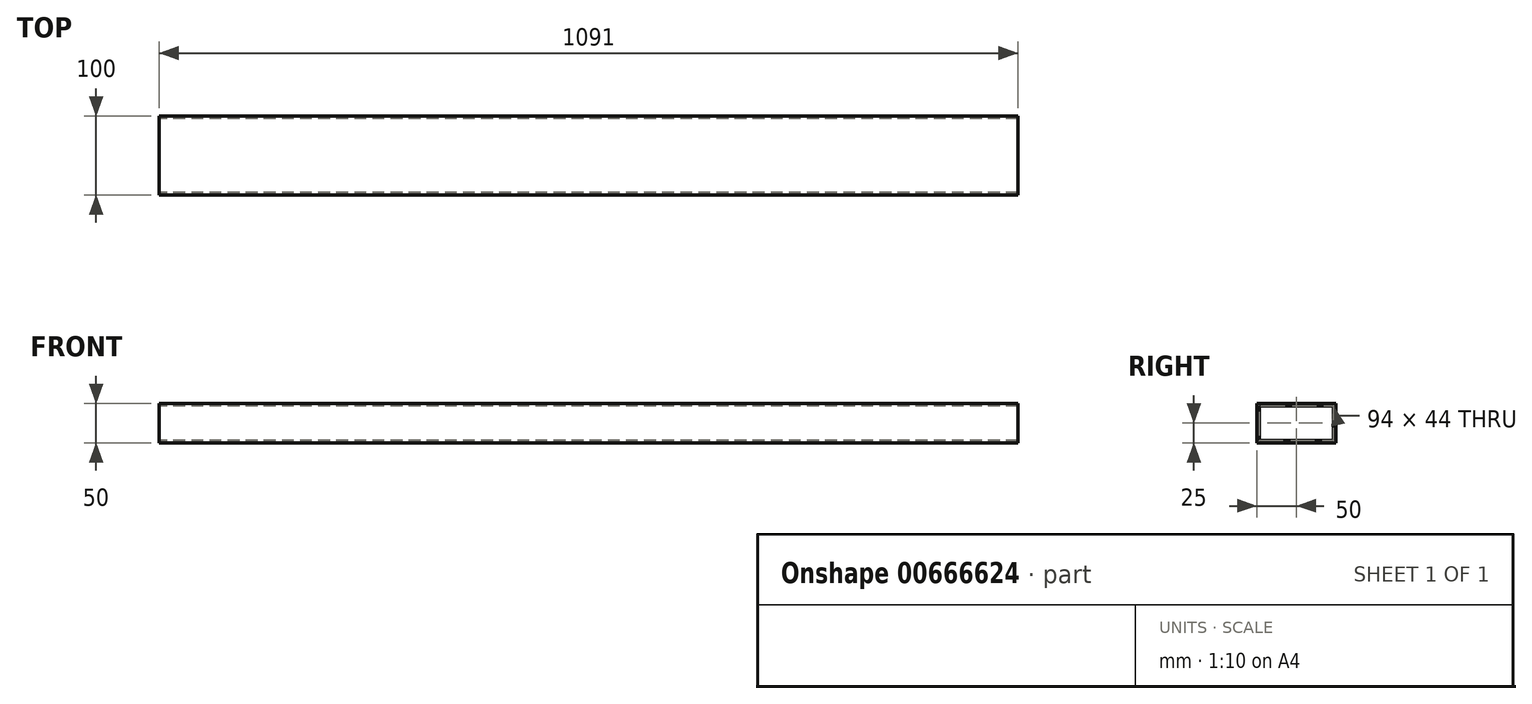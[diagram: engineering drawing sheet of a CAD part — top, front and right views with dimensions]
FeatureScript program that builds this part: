
annotation { "Feature Type Name" : "Feature", "Feature Type Description" : "" }
export const myFeature = defineFeature(function(context is Context, id is Id, definition is map)
    precondition{}
    {
        {
            var Q0;
            Q0=qCreatedBy(makeId("Right.planeOp"),FACE);
            var sketch = newSketch(context, id + "F0", { "sketchPlane" : qUnion([Q0])});
            skLineSegment(sketch, "E0.bottom", {"start": v(50, -25) * mm, "end": v(-50, -25) * mm});
            skLineSegment(sketch, "E0.top", {"start": v(50, 25) * mm, "end": v(-50, 25) * mm});
            skLineSegment(sketch, "E0.left", {"start": v(50, -25) * mm, "end": v(50, 25) * mm});
            skLineSegment(sketch, "E0.right", {"start": v(-50, -25) * mm, "end": v(-50, 25) * mm});
            skPoint(sketch, "E0.middle", {"position": v(0, 0) * mm});
            skLineSegment(sketch, "E1.bottom", {"start": v(47, -22) * mm, "end": v(-47, -22) * mm});
            skLineSegment(sketch, "E1.top", {"start": v(47, 22) * mm, "end": v(-47, 22) * mm});
            skLineSegment(sketch, "E1.left", {"start": v(47, -22) * mm, "end": v(47, 22) * mm});
            skLineSegment(sketch, "E1.right", {"start": v(-47, -22) * mm, "end": v(-47, 22) * mm});
            skSolve(sketch);
        }
        {
            var Q0;
            Q0=makeQuery(id+"F0.imprint","IMPRINT",FACE,{"disambiguationData":[TD([[makeQuery(id+"F0.imprint","IMPRINT",EDGE,{"derivedFrom":sQuery(id+"F0.wireOp",EDGE,"E0.bottom")}),-1.0]])]});
            extrude(context, id + "F1", {"entities" : qUnion([Q0]), "depth" : 1091 * mm, "offsetDistance" : 25 * mm});
        }
    });
